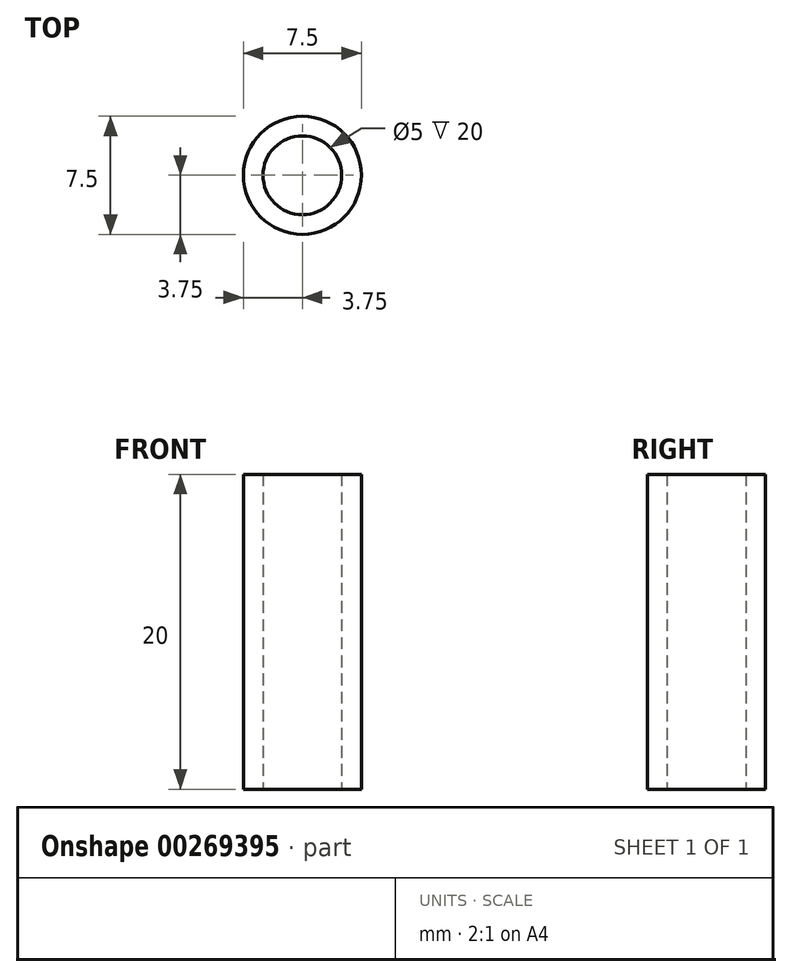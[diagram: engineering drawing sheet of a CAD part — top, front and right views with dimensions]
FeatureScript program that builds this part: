
annotation { "Feature Type Name" : "Feature", "Feature Type Description" : "" }
export const myFeature = defineFeature(function(context is Context, id is Id, definition is map)
    precondition{}
    {
        {
            var Q0;
            Q0=qCreatedBy(makeId("Top.planeOp"),FACE);
            var sketch = newSketch(context, id + "F0", { "sketchPlane" : qUnion([Q0])});
            skCircle(sketch, "E0", {"center": v(0, 0) * mm, "radius": 3.75 * mm});
            skCircle(sketch, "E1", {"center": v(0, 0) * mm, "radius": 2.5 * mm});
            skSolve(sketch);
        }
        {
            var Q0;
            Q0 = qSketchRegion(id + "F0", true);
            extrude(context, id + "F1", {"entities" : qUnion([Q0]), "depth" : 20 * mm});
        }
    });
